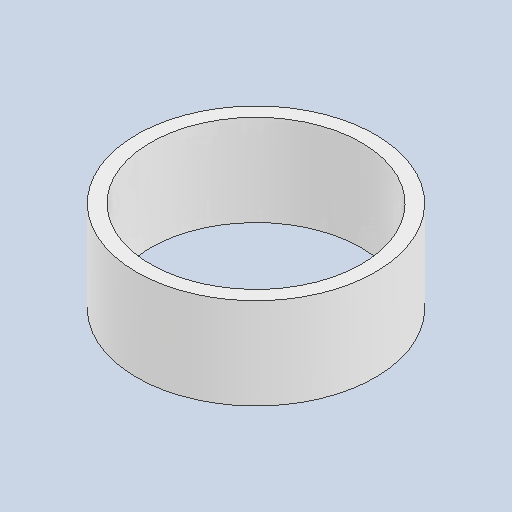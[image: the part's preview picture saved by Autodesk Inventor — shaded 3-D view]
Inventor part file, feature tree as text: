
AUTODESK INVENTOR PART (.ipt)
format: ipt  version: 2023.4 (Build 274418000, 418)  size: 93,696 bytes
history: native  units: mm
features: extrude x1
ambient origin geometry x8: Origin, YZ Plane, XZ Plane, XY Plane, X Axis, Y Axis, Z Axis, Center Point
bodies: Solid1 (feature_tree)
feature tree (1):
  extrude  "Extrude2"  [1 undecoded]
note: 1 required parameter value undecoded (feature->parameter linkage not recoverable at this tier; creation-order binding heuristic only, values carry confidence <= 0.55)
